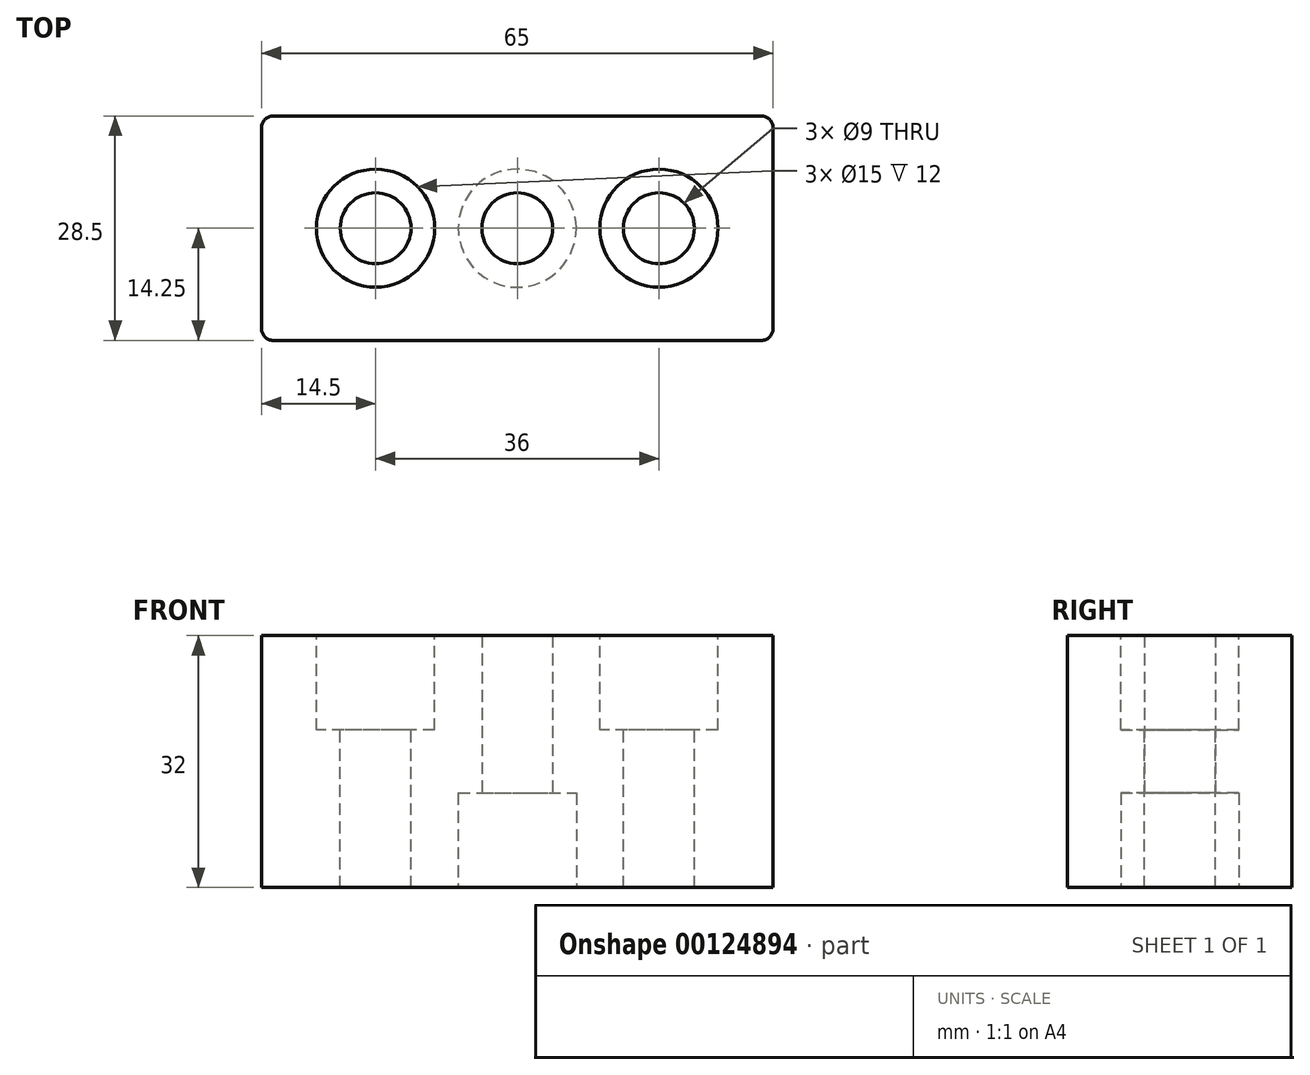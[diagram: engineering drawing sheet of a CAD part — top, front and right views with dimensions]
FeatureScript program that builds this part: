
annotation { "Feature Type Name" : "Feature", "Feature Type Description" : "" }
export const myFeature = defineFeature(function(context is Context, id is Id, definition is map)
    precondition{}
    {
        {
            var Q0;
            Q0=qCreatedBy(makeId("Front.planeOp"),FACE);
            var sketch = newSketch(context, id + "F0", { "sketchPlane" : qUnion([Q0])});
            skLineSegment(sketch, "E0.bottom", {"start": v(32.5, 16) * mm, "end": v(-32.5, 16) * mm});
            skLineSegment(sketch, "E0.top", {"start": v(32.5, -16) * mm, "end": v(-32.5, -16) * mm});
            skLineSegment(sketch, "E0.left", {"start": v(32.5, 16) * mm, "end": v(32.5, -16) * mm});
            skLineSegment(sketch, "E0.right", {"start": v(-32.5, 16) * mm, "end": v(-32.5, -16) * mm});
            skPoint(sketch, "E0.middle", {"position": v(0, 0) * mm});
            skSolve(sketch);
        }
        {
            var Q0;
            Q0=makeQuery(id+"F0.imprint","IMPRINT",FACE,{"disambiguationData":[TD([[makeQuery(id+"F0.imprint","IMPRINT",EDGE,{"derivedFrom":sQuery(id+"F0.wireOp",EDGE,"E0.bottom")}),1.0]])]});
            extrude(context, id + "F1", {"entities" : qUnion([Q0]), "endBound" : BoundingType.SYMMETRIC, "depth" : 28.5 * mm});
        }
        {
            var Q0;
            Q0=makeQuery(id+"F1.opExtrude","SWEPT_FACE",FACE,{"disambiguationData":[OSD([sQuery(id+"F0.wireOp",EDGE,"E0.bottom")])]});
            var sketch = newSketch(context, id + "F2", { "sketchPlane" : qUnion([Q0])});
            skLineSegment(sketch, "E1", {"start": v(0, -14.25) * mm, "end": v(0, 0) * mm});
            skLineSegment(sketch, "E2", {"start": v(0, 0) * mm, "end": v(18, 0) * mm});
            skLineSegment(sketch, "E3.MirrorCS", {"start": v(0, 0) * mm, "end": v(-18, 0) * mm});
            skSolve(sketch);
        }
        {
            var Q0;
            Q0=makeQuery(id+"F1.opExtrude","SWEPT_FACE",FACE,{"disambiguationData":[OSD([sQuery(id+"F0.wireOp",EDGE,"E0.top")])]});
            var sketch = newSketch(context, id + "F3", { "sketchPlane" : qUnion([Q0])});
            skPoint(sketch, "E4", {"position": v(0, 0) * mm});
            skSolve(sketch);
        }
        {
            var Q0;
            Q0=sQuery(id+"F2.wireOp",VERTEX,"E3.MirrorCS.end");
            var Q1;
            Q1=sQuery(id+"F2.wireOp",VERTEX,"E2.end");
            var Q2;
            Q2=sQuery(id+"F3.wireOp",VERTEX,"E4");
            var Q3;
            Q3=makeQuery(id+"F1.opExtrude","SWEPT_BODY",BODY,{"disambiguationData":[OSD([sQuery(id+"F0.wireOp",EDGE,"E0.bottom"),sQuery(id+"F0.wireOp",EDGE,"E0.top"),sQuery(id+"F0.wireOp",EDGE,"E0.left"),sQuery(id+"F0.wireOp",EDGE,"E0.right")])]});
            hole(context, id + "F4", {"style" : HoleStyle.C_BORE, "endStyle" : HoleEndStyle.BLIND, "holeDiameter" : 9 * mm, "cBoreDiameter" : 15 * mm, "cBoreDepth" : 12 * mm, "holeDepth" : 40 * mm, "startFromSketch" : true, "locations" : qUnion([Q0, Q1, Q2]), "scope" : qUnion([Q3])});
        }
        {
            var Q0;
            Q0=makeQuery(id+"F1.opExtrude","CAP_EDGE",EDGE,{"disambiguationData":[OSD([sQuery(id+"F0.wireOp",EDGE,"E0.right")])],"isStart":false});
            var Q1;
            Q1=makeQuery(id+"F1.opExtrude","CAP_EDGE",EDGE,{"disambiguationData":[OSD([sQuery(id+"F0.wireOp",EDGE,"E0.left")])],"isStart":false});
            var Q2;
            Q2=makeQuery(id+"F1.opExtrude","CAP_EDGE",EDGE,{"disambiguationData":[OSD([sQuery(id+"F0.wireOp",EDGE,"E0.left")])],"isStart":true});
            var Q3;
            Q3=makeQuery(id+"F1.opExtrude","CAP_EDGE",EDGE,{"disambiguationData":[OSD([sQuery(id+"F0.wireOp",EDGE,"E0.right")])],"isStart":true});
            fillet(context, id + "F5", {"entities" : qUnion([Q0, Q1, Q2, Q3]), "radius" : 1.5 * mm, "tangentPropagation" : true, "allowEdgeOverflow" : false});
        }
    });
